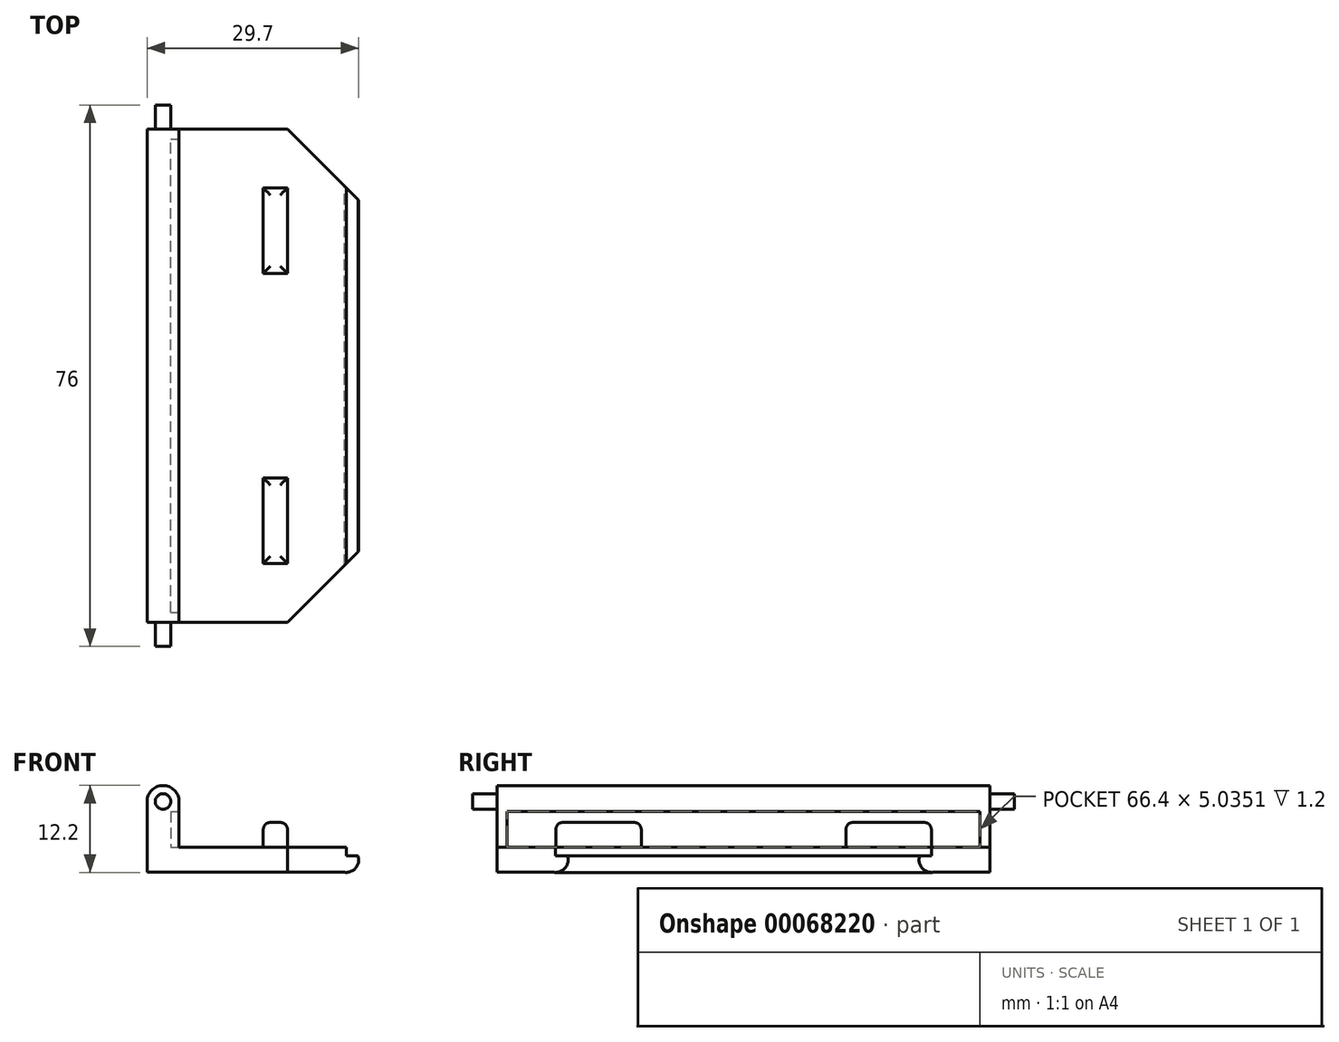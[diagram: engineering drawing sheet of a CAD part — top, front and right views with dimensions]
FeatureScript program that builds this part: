
annotation { "Feature Type Name" : "Feature", "Feature Type Description" : "" }
export const myFeature = defineFeature(function(context is Context, id is Id, definition is map)
    precondition{}
    {
        {
            var Q0;
            Q0=qCreatedBy(makeId("Front.planeOp"),FACE);
            var sketch = newSketch(context, id + "F0", { "sketchPlane" : qUnion([Q0])});
            skLineSegment(sketch, "E0", {"start": v(-16.77, 9.94) * mm, "end": v(-16.77, 0) * mm});
            skLineSegment(sketch, "E1", {"start": v(-16.77, 0) * mm, "end": v(10.96, 0) * mm});
            skLineSegment(sketch, "E2.0", {"start": v(-12.27, 3.5) * mm, "end": v(11.18, 3.5) * mm});
            skLineSegment(sketch, "E2.1", {"start": v(-12.27, 9.94) * mm, "end": v(-12.27, 3.5) * mm});
            skArc(sketch, "E3", {"start": v(-12.27, 9.94) * mm, "mid": v(-14.52, 12.19) * mm, "end": v(-16.77, 9.94) * mm});
            skArc(sketch, "E4", {"start": v(10.96, 0) * mm, "mid": v(12.93, 1.64) * mm, "end": v(11.18, 3.5) * mm});
            skCircle(sketch, "E5", {"center": v(-14.52, 9.94) * mm, "radius": 1.1 * mm});
            skSolve(sketch);
        }
        {
            var Q0;
            Q0 = qSketchRegion(id + "F0", true);
            extrude(context, id + "F1", {"entities" : qUnion([Q0]), "depth" : 34.6 * mm, "hasSecondDirection" : true, "secondDirectionOppositeDirection" : true, "secondDirectionDepth" : 34.6 * mm});
        }
        {
            var Q0;
            Q0=makeQuery(id+"F0.imprint","IMPRINT",FACE,{"disambiguationData":[TD([[makeQuery(id+"F0.imprint","IMPRINT",EDGE,{"derivedFrom":sQuery(id+"F0.wireOp",EDGE,"E5")}),1.0]])]});
            extrude(context, id + "F2", {"entities" : qUnion([Q0]), "operationType" : NewBodyOperationType.ADD, "depth" : 38 * mm, "hasSecondDirection" : true, "secondDirectionOppositeDirection" : true, "secondDirectionDepth" : 38 * mm});
        }
        {
            var Q0;
            Q0=makeQuery(id+"F1.opExtrude","SWEPT_FACE",FACE,{"disambiguationData":[OSD([sQuery(id+"F0.wireOp",EDGE,"E2.1")])]});
            var sketch = newSketch(context, id + "F3", { "sketchPlane" : qUnion([Q0])});
            skLineSegment(sketch, "E6.bottom", {"start": v(-34.6, 9.94) * mm, "end": v(34.6, 9.94) * mm});
            skLineSegment(sketch, "E6.top", {"start": v(-34.6, 3.5) * mm, "end": v(34.6, 3.5) * mm});
            skLineSegment(sketch, "E6.left", {"start": v(-34.6, 9.94) * mm, "end": v(-34.6, 3.5) * mm});
            skLineSegment(sketch, "E6.right", {"start": v(34.6, 9.94) * mm, "end": v(34.6, 3.5) * mm});
            skLineSegment(sketch, "E7.0", {"start": v(33.2, 8.54) * mm, "end": v(33.2, 3.5) * mm});
            skLineSegment(sketch, "E7.1", {"start": v(-33.2, 8.54) * mm, "end": v(33.2, 8.54) * mm});
            skLineSegment(sketch, "E7.2", {"start": v(-33.2, 8.54) * mm, "end": v(-33.2, 4.5) * mm});
            skLineSegment(sketch, "E8", {"start": v(-33.2, 4.5) * mm, "end": v(-33.2, 3.5) * mm});
            skSolve(sketch);
        }
        {
            var Q0;
            {var subQ0=sQuery(id+"F3.wireOp",EDGE,"E7.0");Q0=makeQuery(id+"F3.imprint","IMPRINT",FACE,{"disambiguationData":[TD([[makeQuery(id+"F3.imprint","IMPRINT",EDGE,{"derivedFrom":subQ0}),-1.0]])]});}
            extrude(context, id + "F4", {"entities" : qUnion([Q0]), "operationType" : NewBodyOperationType.REMOVE, "oppositeDirection" : true, "depth" : 1.2 * mm});
        }
        {
            var Q0;
            Q0=makeQuery(id+"F4.boolean.opBoolean","MERGE",FACE,{"derivedFrom":[makeQuery(id+"F1.opExtrude","SWEPT_FACE",FACE,{"disambiguationData":[OSD([sQuery(id+"F0.wireOp",EDGE,"E2.0")])]}),makeQuery(id+"F4.opExtrude","SWEPT_FACE",FACE,{"disambiguationData":[OSD([sQuery(id+"F3.wireOp",EDGE,"E6.top")])]})]});
            var sketch = newSketch(context, id + "F5", { "sketchPlane" : qUnion([Q0])});
            skLineSegment(sketch, "E9.bottom", {"start": v(-12.27, 34.6) * mm, "end": v(12.94, 34.6) * mm});
            skLineSegment(sketch, "E9.top", {"start": v(-12.27, -34.6) * mm, "end": v(12.94, -34.6) * mm});
            skLineSegment(sketch, "E9.left", {"start": v(-12.27, 33.2) * mm, "end": v(-12.27, -34.6) * mm});
            skLineSegment(sketch, "E9.right", {"start": v(12.94, 34.6) * mm, "end": v(12.94, -34.6) * mm});
            skLineSegment(sketch, "E10.2", {"start": v(-12.27, -33.2) * mm, "end": v(4.34, -33.2) * mm});
            skLineSegment(sketch, "E11", {"start": v(-12.27, -33.2) * mm, "end": v(-12.27, 33.2) * mm});
            skLineSegment(sketch, "E12", {"start": v(-12.27, 33.2) * mm, "end": v(-12.27, 33.2) * mm});
            skLineSegment(sketch, "E13", {"start": v(2.94, 48.4) * mm, "end": v(2.94, -38.09) * mm, "construction": true});
            skLineSegment(sketch, "E14", {"start": v(2.94, 34.6) * mm, "end": v(12.94, 24.6) * mm});
            skLineSegment(sketch, "E15.MirrorCS", {"start": v(2.94, -34.6) * mm, "end": v(12.94, -24.6) * mm});
            skLineSegment(sketch, "E16.bottom", {"start": v(2.94, 26.35) * mm, "end": v(-0.46, 26.35) * mm});
            skLineSegment(sketch, "E16.top", {"start": v(2.94, 14.35) * mm, "end": v(-0.46, 14.35) * mm});
            skLineSegment(sketch, "E16.left", {"start": v(2.94, 26.35) * mm, "end": v(2.94, 14.35) * mm});
            skLineSegment(sketch, "E16.right", {"start": v(-0.46, 26.35) * mm, "end": v(-0.46, 14.35) * mm});
            skLineSegment(sketch, "E17.MirrorCS", {"start": v(2.94, -14.35) * mm, "end": v(-0.46, -14.35) * mm});
            skLineSegment(sketch, "E18.MirrorCS", {"start": v(-0.46, -26.35) * mm, "end": v(-0.46, -14.35) * mm});
            skLineSegment(sketch, "E19.MirrorCS", {"start": v(2.94, -26.35) * mm, "end": v(2.94, -14.35) * mm});
            skLineSegment(sketch, "E20.MirrorCS", {"start": v(2.94, -26.35) * mm, "end": v(-0.46, -26.35) * mm});
            skLineSegment(sketch, "E21", {"start": v(-12.27, 33.2) * mm, "end": v(4.34, 33.2) * mm});
            skSolve(sketch);
        }
        {
            var Q0;
            {var subQ1=sQuery(id+"F5.wireOp",EDGE,"E11");Q0=makeQuery(id+"F5.imprint","IMPRINT",FACE,{"disambiguationData":[TD([[makeQuery(id+"F5.imprint","IMPRINT",EDGE,{"derivedFrom":subQ1}),-1.0]])]});}
            var Q1;
            Q1=makeQuery(id+"F5.imprint","IMPRINT",FACE,{"disambiguationData":[TD([[makeQuery(id+"F5.imprint","IMPRINT",EDGE,{"derivedFrom":sQuery(id+"F5.wireOp",EDGE,"E12")}),-1.0]])]});
            var Q2;
            {var subQ0=sQuery(id+"F5.wireOp",EDGE,"E10.0");var subQ1=sQuery(id+"F5.wireOp",EDGE,"E9.right");var subQ2=makeQuery(id+"F5.imprint","INTERSECT",VERTEX,{"derivedFrom":[subQ1,subQ0]});Q2=makeQuery(id+"F5.imprint","IMPRINT",FACE,{"disambiguationData":[TD([[makeQuery(id+"F5.imprint","IMPRINT",EDGE,{"disambiguationData":[TD([[subQ2,-1.0]])],"derivedFrom":subQ1}),-1.0]])]});}
            var Q3;
            Q3=makeQuery(id+"F5.imprint","IMPRINT",FACE,{"disambiguationData":[TD([[makeQuery(id+"F5.imprint","IMPRINT",EDGE,{"derivedFrom":sQuery(id+"F5.wireOp",EDGE,"E11")}),1.0]])]});
            extrude(context, id + "F6", {"entities" : qUnion([Q0, Q1, Q2, Q3]), "operationType" : NewBodyOperationType.REMOVE, "oppositeDirection" : true, "depth" : 1.2 * mm});
        }
        {
            var Q0;
            {var subQ3=sQuery(id+"F5.wireOp",EDGE,"E14");var subQ5=makeQuery(id+"F5.imprint","INTERSECT",VERTEX,{"derivedFrom":[sQuery(id+"F5.wireOp",EDGE,"E10.0"),subQ3]});Q0=makeQuery(id+"F5.imprint","IMPRINT",FACE,{"disambiguationData":[TD([[makeQuery(id+"F5.imprint","IMPRINT",EDGE,{"disambiguationData":[TD([[subQ5,1.0]])],"derivedFrom":subQ3}),1.0]])]});}
            var Q1;
            {var subQ0=sQuery(id+"F5.wireOp",EDGE,"E9.bottom");var subQ3=sQuery(id+"F5.wireOp",EDGE,"E9.right");var subQ4=makeQuery(id+"F5.imprint","INTERSECT",VERTEX,{"derivedFrom":[subQ0,subQ3]});Q1=makeQuery(id+"F5.imprint","IMPRINT",FACE,{"disambiguationData":[TD([[makeQuery(id+"F5.imprint","IMPRINT",EDGE,{"disambiguationData":[TD([[subQ4,-1.0]])],"derivedFrom":subQ3}),-1.0]])]});}
            var Q2;
            {var subQ0=sQuery(id+"F5.wireOp",EDGE,"E9.top");var subQ3=sQuery(id+"F5.wireOp",EDGE,"E9.right");var subQ4=makeQuery(id+"F5.imprint","INTERSECT",VERTEX,{"derivedFrom":[subQ0,subQ3]});Q2=makeQuery(id+"F5.imprint","IMPRINT",FACE,{"disambiguationData":[TD([[makeQuery(id+"F5.imprint","IMPRINT",EDGE,{"disambiguationData":[TD([[subQ4,1.0]])],"derivedFrom":subQ3}),-1.0]])]});}
            var Q3;
            {var subQ3=sQuery(id+"F5.wireOp",EDGE,"E15.MirrorCS");var subQ5=makeQuery(id+"F5.imprint","INTERSECT",VERTEX,{"derivedFrom":[sQuery(id+"F5.wireOp",EDGE,"E10.2"),subQ3]});Q3=makeQuery(id+"F5.imprint","IMPRINT",FACE,{"disambiguationData":[TD([[makeQuery(id+"F5.imprint","IMPRINT",EDGE,{"disambiguationData":[TD([[subQ5,1.0]])],"derivedFrom":subQ3}),-1.0]])]});}
            extrude(context, id + "F7", {"entities" : qUnion([Q0, Q1, Q2, Q3]), "operationType" : NewBodyOperationType.REMOVE, "oppositeDirection" : true, "depth" : 5 * mm, "hasSecondDirection" : true, "secondDirectionOppositeDirection" : false, "secondDirectionDepth" : 5 * mm});
        }
        {
            var Q0;
            Q0=makeQuery(id+"F5.imprint","IMPRINT",FACE,{"disambiguationData":[TD([[makeQuery(id+"F5.imprint","IMPRINT",EDGE,{"derivedFrom":sQuery(id+"F5.wireOp",EDGE,"E16.bottom")}),1.0]])]});
            var Q1;
            Q1=makeQuery(id+"F5.imprint","IMPRINT",FACE,{"disambiguationData":[TD([[makeQuery(id+"F5.imprint","IMPRINT",EDGE,{"derivedFrom":sQuery(id+"F5.wireOp",EDGE,"E17.MirrorCS")}),1.0]])]});
            extrude(context, id + "F8", {"entities" : qUnion([Q0, Q1]), "operationType" : NewBodyOperationType.ADD, "depth" : 3.5 * mm});
        }
        {
            var Q0;
            Q0=makeQuery(id+"F8.opExtrude","CAP_FACE",FACE,{"disambiguationData":[OSD([sQuery(id+"F5.wireOp",EDGE,"E17.MirrorCS"),sQuery(id+"F5.wireOp",EDGE,"E18.MirrorCS"),sQuery(id+"F5.wireOp",EDGE,"E19.MirrorCS"),sQuery(id+"F5.wireOp",EDGE,"E20.MirrorCS")])],"isStart":false});
            var Q1;
            Q1=makeQuery(id+"F8.opExtrude","CAP_FACE",FACE,{"disambiguationData":[OSD([sQuery(id+"F5.wireOp",EDGE,"E16.bottom"),sQuery(id+"F5.wireOp",EDGE,"E16.top"),sQuery(id+"F5.wireOp",EDGE,"E16.left"),sQuery(id+"F5.wireOp",EDGE,"E16.right")])],"isStart":false});
            fillet(context, id + "F9", {"entities" : qUnion([Q0, Q1]), "radius" : 1 * mm, "tangentPropagation" : true, "allowEdgeOverflow" : false});
        }
    });
